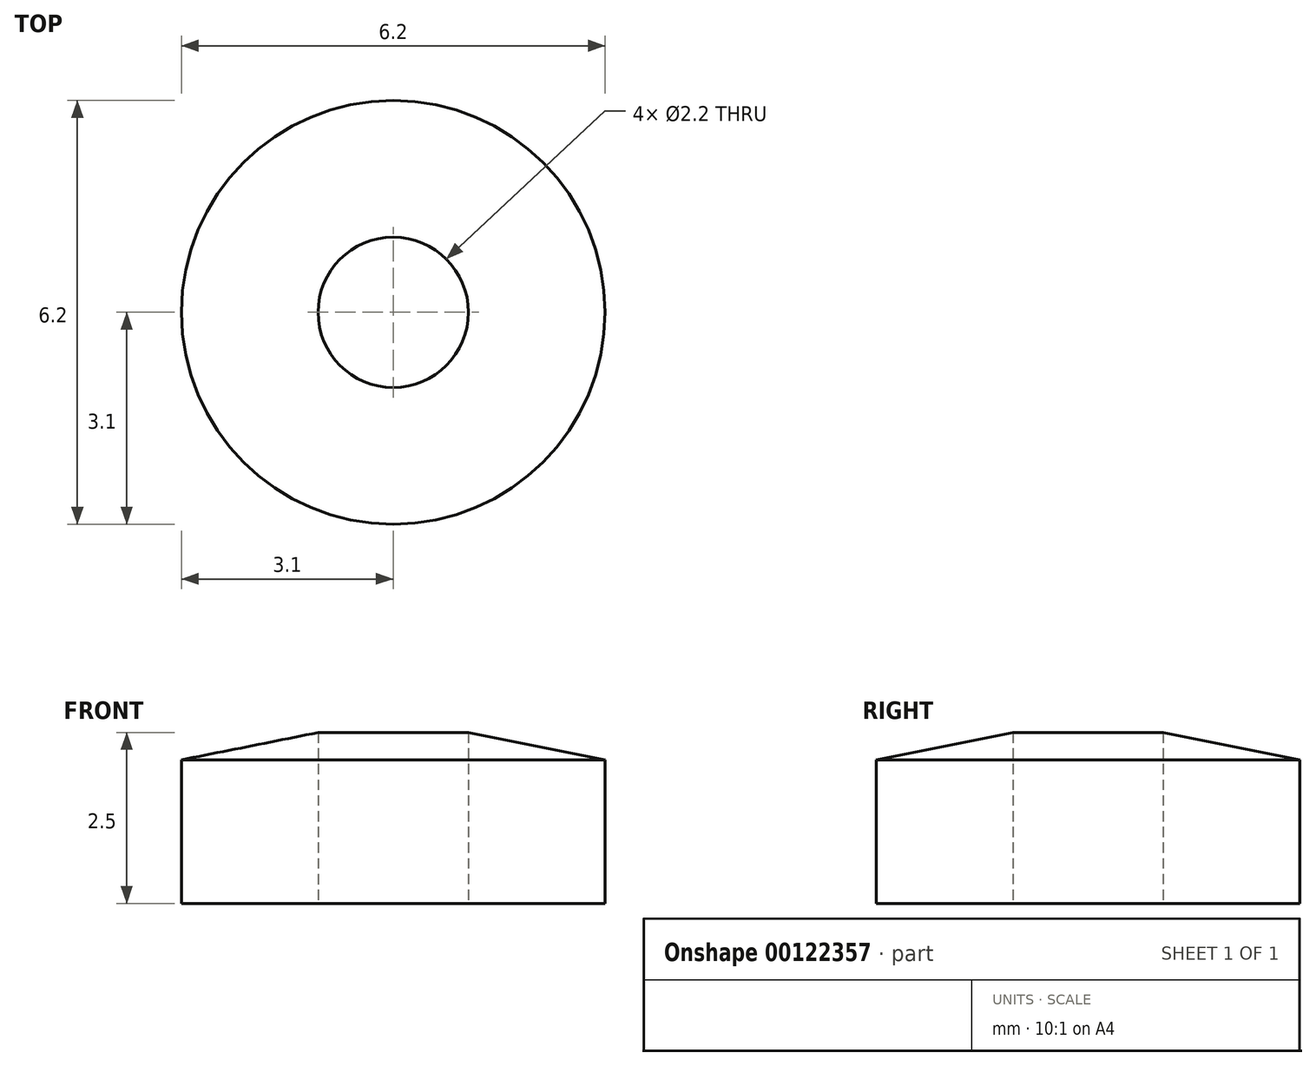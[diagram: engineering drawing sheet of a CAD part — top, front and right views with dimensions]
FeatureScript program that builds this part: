
annotation { "Feature Type Name" : "Feature", "Feature Type Description" : "" }
export const myFeature = defineFeature(function(context is Context, id is Id, definition is map)
    precondition{}
    {
        {
            var Q0;
            Q0=qCreatedBy(makeId("Front.planeOp"),FACE);
            var sketch = newSketch(context, id + "F0", { "sketchPlane" : qUnion([Q0])});
            skLineSegment(sketch, "E0", {"start": v(1.1, 0) * mm, "end": v(1.1, 2.5) * mm});
            skLineSegment(sketch, "E1", {"start": v(1.1, 2.5) * mm, "end": v(3.1, 2.1) * mm});
            skLineSegment(sketch, "E2", {"start": v(3.1, 2.1) * mm, "end": v(3.1, 0) * mm});
            skLineSegment(sketch, "E3", {"start": v(3.1, 0) * mm, "end": v(1.1, 0) * mm});
            skLineSegment(sketch, "E4", {"start": v(0, 0) * mm, "end": v(0, 1.2) * mm, "construction": true});
            skSolve(sketch);
        }
        {
            var Q0;
            Q0=makeQuery(id+"F0.imprint","IMPRINT",FACE,{"disambiguationData":[TD([[makeQuery(id+"F0.imprint","IMPRINT",EDGE,{"derivedFrom":sQuery(id+"F0.wireOp",EDGE,"E0")}),-1.0]])]});
            var Q1;
            Q1=sQuery(id+"F0.wireOp",EDGE,"E4");
            revolve(context, id + "F1", {"entities" : qUnion([Q0]), "axis" : qUnion([Q1]), "revolveType" : RevolveType.FULL});
        }
    });
